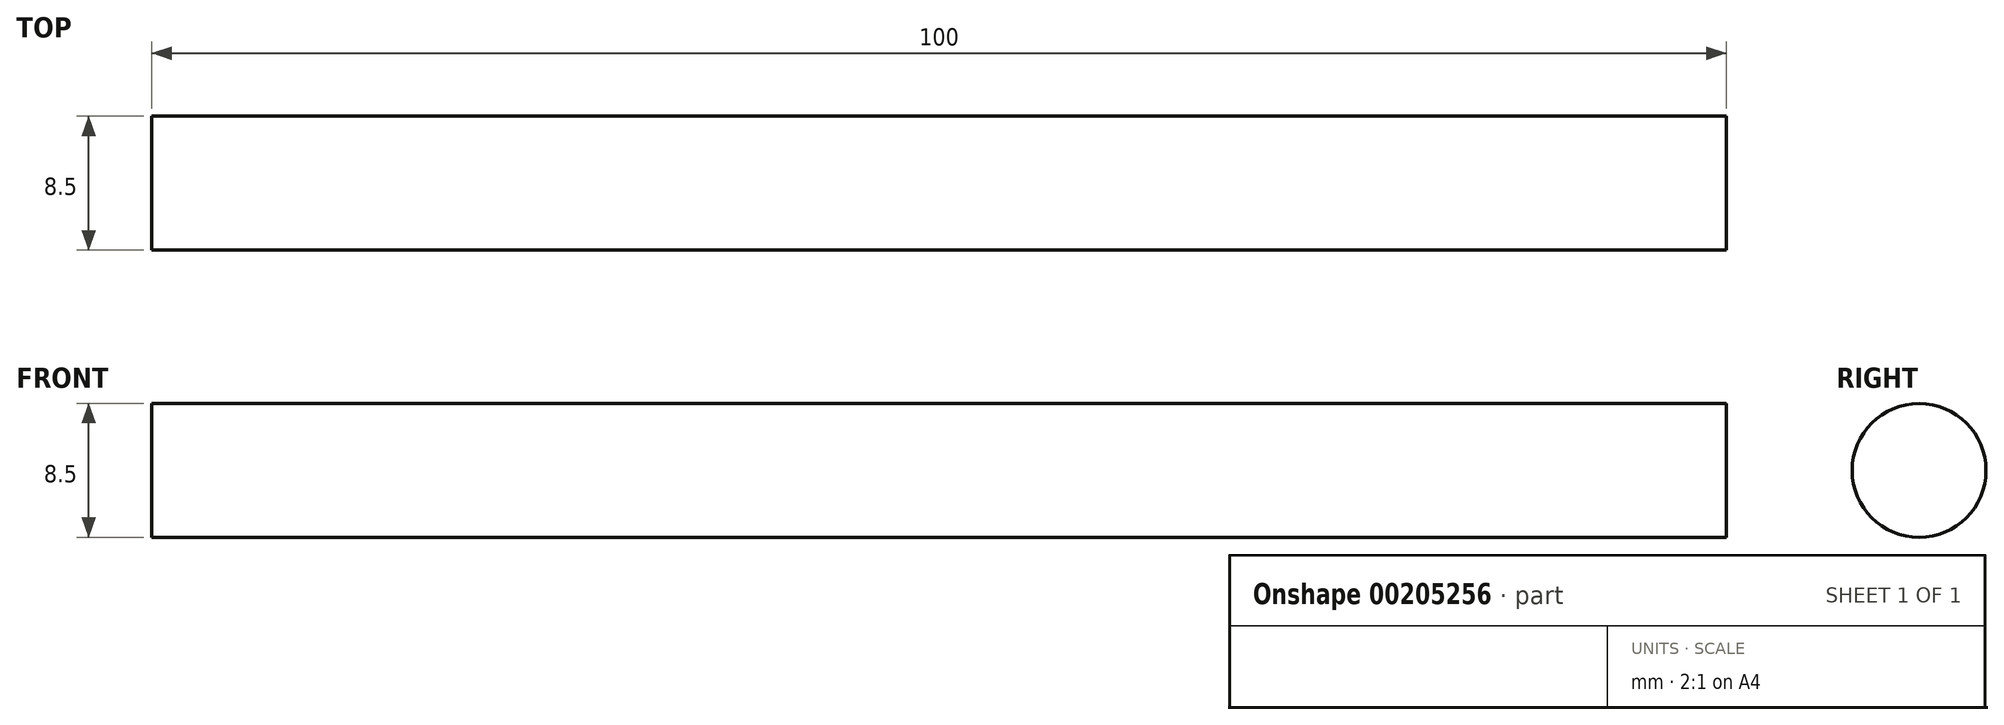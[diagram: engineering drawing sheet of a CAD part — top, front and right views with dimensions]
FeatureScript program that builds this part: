
annotation { "Feature Type Name" : "Feature", "Feature Type Description" : "" }
export const myFeature = defineFeature(function(context is Context, id is Id, definition is map)
    precondition{}
    {
        {
            var Q0;
            Q0=qCreatedBy(makeId("Right.planeOp"),FACE);
            var sketch = newSketch(context, id + "F0", { "sketchPlane" : qUnion([Q0])});
            skCircle(sketch, "E0", {"center": v(0, 0) * mm, "radius": 4.25 * mm});
            skSolve(sketch);
        }
        {
            var Q0;
            Q0=makeQuery(id+"F0.imprint","IMPRINT",FACE,{"disambiguationData":[TD([[makeQuery(id+"F0.imprint","IMPRINT",EDGE,{"derivedFrom":sQuery(id+"F0.wireOp",EDGE,"E0")}),1.0]])]});
            extrude(context, id + "F1", {"entities" : qUnion([Q0]), "depth" : 100 * mm});
        }
    });
